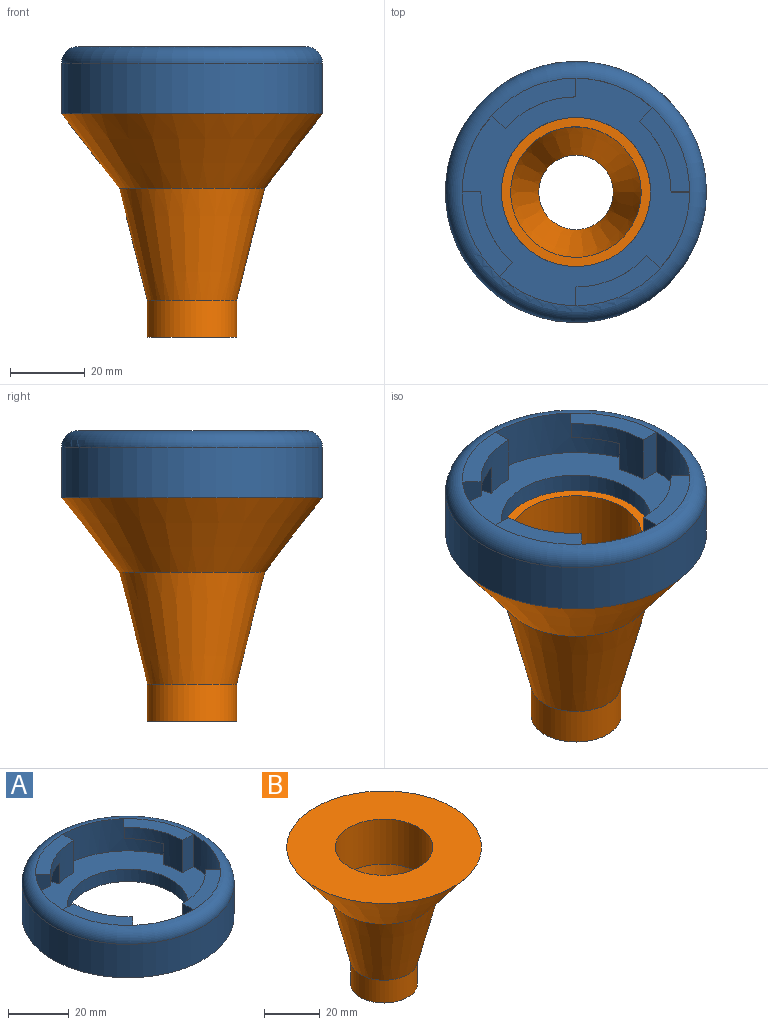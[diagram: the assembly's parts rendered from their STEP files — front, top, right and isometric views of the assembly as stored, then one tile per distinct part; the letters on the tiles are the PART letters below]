
ASSEMBLY  parts=2 mates=1
PART A: 33 faces, bbox 75.8x75.8x18 mm
  f0: plane 22.67x13.44mm, normal (0,0,1), area 117.3mm2, adj f12,f19,f27,f32
  f1: plane 22.67x13.44mm, normal (0,0,1), area 117.3mm2, adj f11,f22,f28,f32
  f2: plane 22.67x13.44mm, normal (0,0,1), area 117.3mm2, adj f10,f24,f29,f32
  f3: cylinder r=35mm len=70mm, axis (0,0,1), area 2968.8mm2, adj f31,f32
  f4: cone r=30.5mm half-angle=60deg, axis (0,0,-1), area 84.6mm2, adj f10,f13,f23,f29
  f5: cone r=30.5mm half-angle=60deg, axis (0,0,-1), area 84.6mm2, adj f11,f14,f21,f28
  f6: cone r=30.5mm half-angle=60deg, axis (0,0,-1), area 84.6mm2, adj f12,f15,f20,f27
  f7: cone r=30.5mm half-angle=60deg, axis (0,0,-1), area 84.6mm2, adj f9,f16,f25,f30
  f8: plane 22.67x13.44mm, normal (0,0,1), area 117.3mm2, adj f9,f26,f30,f32
  f9: cylinder r=25.5mm len=18.95mm, axis (0,0,1), area 165.7mm2, adj f7,f8,f17,f25,f26,f30
  f10: cylinder r=25.5mm len=18.95mm, axis (0,0,1), area 165.7mm2, adj f2,f4,f17,f23,f24,f29
  f11: cylinder r=25.5mm len=18.95mm, axis (0,0,1), area 165.7mm2, adj f1,f5,f17,f21,f22,f28
  f12: cylinder r=25.5mm len=18.95mm, axis (0,0,1), area 165.7mm2, adj f0,f6,f17,f19,f20,f27
  f13: cylinder r=30.5mm len=29.01mm, axis (0,0,1), area 378.5mm2, adj f4,f17,f23,f26,f29,f32
  f14: cylinder r=30.5mm len=29.01mm, axis (0,0,1), area 378.5mm2, adj f5,f17,f21,f24,f28,f32
  f15: cylinder r=30.5mm len=29.01mm, axis (0,0,1), area 378.5mm2, adj f6,f17,f20,f22,f27,f32
  f16: cylinder r=30.5mm len=29.01mm, axis (0,0,1), area 378.5mm2, adj f7,f17,f19,f25,f30,f32
  f17: plane 61x61mm, normal (0,0,1), area 1489.9mm2, adj f9,f10,f11,f12,f13,f14,f15,f16
  f18: cylinder r=20mm len=40mm, axis (0,0,1), area 628.3mm2, adj f17,f31
  f19: plane 13x5mm, normal (0,-1,0), area 65mm2, adj f0,f12,f16,f17
  f20: plane 8.39x4.76mm, normal (-0.31,0.95,0), area 34.7mm2, adj f6,f12,f15,f17
  f21: plane 8.39x4.76mm, normal (-0.95,-0.31,0), area 34.7mm2, adj f5,f11,f14,f17
  f22: plane 13x5mm, normal (1,0,0), area 65mm2, adj f1,f11,f15,f17
  f23: plane 8.39x4.76mm, normal (0.31,-0.95,0), area 34.7mm2, adj f4,f10,f13,f17
  f24: plane 13x5mm, normal (0,1,0), area 65mm2, adj f2,f10,f14,f17
  f25: plane 8.39x4.76mm, normal (0.95,0.31,0), area 34.7mm2, adj f7,f9,f16,f17
  f26: plane 13x5mm, normal (-1,0,0), area 65mm2, adj f8,f9,f13,f17
  f27: plane 7.5x3.72mm, normal (-0.74,0.67,0), area 30.3mm2, adj f0,f6,f12,f15
  f28: plane 7.5x3.72mm, normal (-0.67,-0.74,0), area 30.3mm2, adj f1,f5,f11,f14
  f29: plane 7.5x3.72mm, normal (0.74,-0.67,0), area 30.3mm2, adj f2,f4,f10,f13
  f30: plane 7.5x3.72mm, normal (0.67,0.74,0), area 30.3mm2, adj f7,f8,f9,f16
  f31: plane 70x70mm, normal (0,0,-1), area 2591.8mm2, adj f3,f18
  f32: torus R=30.5mm, axis (0,0,1), area 1481.8mm2, adj f0,f1,f2,f3,f8,f13,f14,f15
PART B: 8 faces, bbox 70x70x60 mm
  f0: plane 70x70mm, normal (0,0,1), area 2886.3mm2, adj f1,f7
  f1: cylinder r=17.5mm len=35mm, axis (0,0,1), area 2172mm2, adj f0,f2
  f2: cone r=17.5mm half-angle=14deg, axis (0,0,1), area 2671.6mm2, adj f1,f3
  f3: cylinder r=10mm len=20mm, axis (0,0,1), area 643.8mm2, adj f2,f4
  f4: plane 24x24mm, normal (0,0,-1), area 138.2mm2, adj f3,f5
  f5: cylinder r=12mm len=24mm, axis (0,0,1), area 754mm2, adj f4,f6
  f6: cone r=12mm half-angle=14deg, axis (0,0,1), area 3060.2mm2, adj f5,f7
  f7: cone r=35mm half-angle=37.8deg, axis (0,0,1), area 4332.3mm2, adj f0,f6
PLACE A t=(7.83,-16.35,26.7)mm
PLACE B t=(7.83,-16.35,-31.3)mm
MATE fastened A.f3 <-> B.f1  axis (0,0,-1) through (7.83,-16.35,28.7)mm
